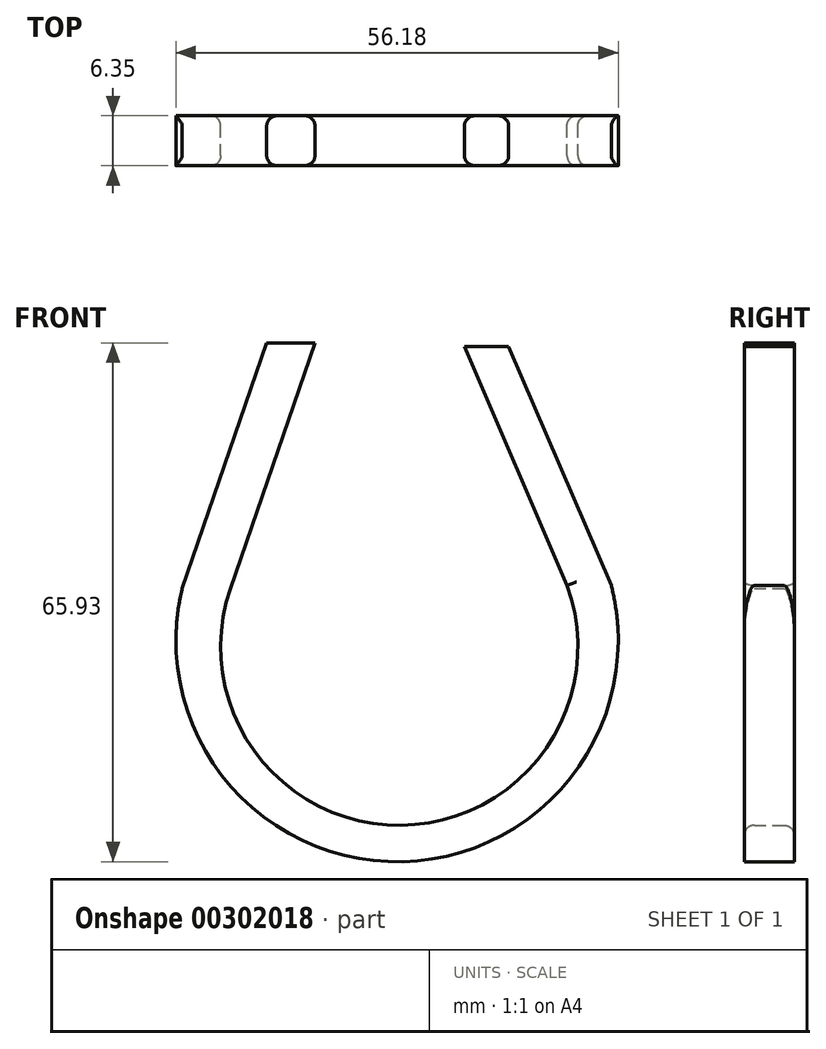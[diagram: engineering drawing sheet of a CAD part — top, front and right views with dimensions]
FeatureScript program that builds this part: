
annotation { "Feature Type Name" : "Feature", "Feature Type Description" : "" }
export const myFeature = defineFeature(function(context is Context, id is Id, definition is map)
    precondition{}
    {
        {
            var Q0;
            Q0=qCreatedBy(makeId("Front.planeOp"),FACE);
            var sketch = newSketch(context, id + "F0", { "sketchPlane" : qUnion([Q0])});
            skLineSegment(sketch, "E0", {"start": v(-28.57, 26.7) * mm, "end": v(-39.31, -4.53) * mm});
            skLineSegment(sketch, "E1", {"start": v(2.15, 26.2) * mm, "end": v(15.19, -4.14) * mm});
            skArc(sketch, "E2", {"start": v(-39.31, -4.53) * mm, "mid": v(-11.81, -39.24) * mm, "end": v(15.19, -4.14) * mm});
            skLineSegment(sketch, "E3", {"start": v(-22.45, 26.7) * mm, "end": v(-33.19, -4.53) * mm});
            skLineSegment(sketch, "E4", {"start": v(-3.45, 26.2) * mm, "end": v(9.58, -4.14) * mm});
            skArc(sketch, "E5", {"start": v(-33.19, -4.53) * mm, "mid": v(-11.53, -34.6) * mm, "end": v(9.58, -4.14) * mm});
            skLineSegment(sketch, "E6", {"start": v(-28.57, 26.7) * mm, "end": v(-22.45, 26.7) * mm});
            skLineSegment(sketch, "E7", {"start": v(-3.45, 26.2) * mm, "end": v(2.15, 26.2) * mm});
            skSolve(sketch);
        }
        {
            var Q0;
            Q0 = qSketchRegion(id + "F0", true);
            extrude(context, id + "F1", {"entities" : qUnion([Q0]), "depth" : 6.35 * mm});
        }
        {
            var Q0;
            Q0=makeQuery(id+"F1.opExtrude","CAP_EDGE",EDGE,{"disambiguationData":[OSD([sQuery(id+"F0.wireOp",EDGE,"E0")])],"isStart":false});
            var Q1;
            Q1=makeQuery(id+"F1.opExtrude","CAP_EDGE",EDGE,{"disambiguationData":[OSD([sQuery(id+"F0.wireOp",EDGE,"E1")])],"isStart":false});
            var Q2;
            Q2=makeQuery(id+"F1.opExtrude","CAP_EDGE",EDGE,{"disambiguationData":[OSD([sQuery(id+"F0.wireOp",EDGE,"E1")])],"isStart":true});
            var Q3;
            Q3=makeQuery(id+"F1.opExtrude","CAP_EDGE",EDGE,{"disambiguationData":[OSD([sQuery(id+"F0.wireOp",EDGE,"E0")])],"isStart":true});
            var Q4;
            Q4=makeQuery(id+"F1.opExtrude","CAP_EDGE",EDGE,{"disambiguationData":[OSD([sQuery(id+"F0.wireOp",EDGE,"E3")])],"isStart":false});
            var Q5;
            Q5=makeQuery(id+"F1.opExtrude","CAP_EDGE",EDGE,{"disambiguationData":[OSD([sQuery(id+"F0.wireOp",EDGE,"E4")])],"isStart":true});
            var Q6;
            Q6=makeQuery(id+"F1.opExtrude","CAP_EDGE",EDGE,{"disambiguationData":[OSD([sQuery(id+"F0.wireOp",EDGE,"E4")])],"isStart":false});
            var Q7;
            Q7=makeQuery(id+"F1.opExtrude","CAP_EDGE",EDGE,{"disambiguationData":[OSD([sQuery(id+"F0.wireOp",EDGE,"E3")])],"isStart":true});
            fillet(context, id + "F2", {"entities" : qUnion([Q0, Q1, Q2, Q3, Q4, Q5, Q6, Q7]), "radius" : 1.27 * mm, "tangentPropagation" : true, "allowEdgeOverflow" : false});
        }
    });
